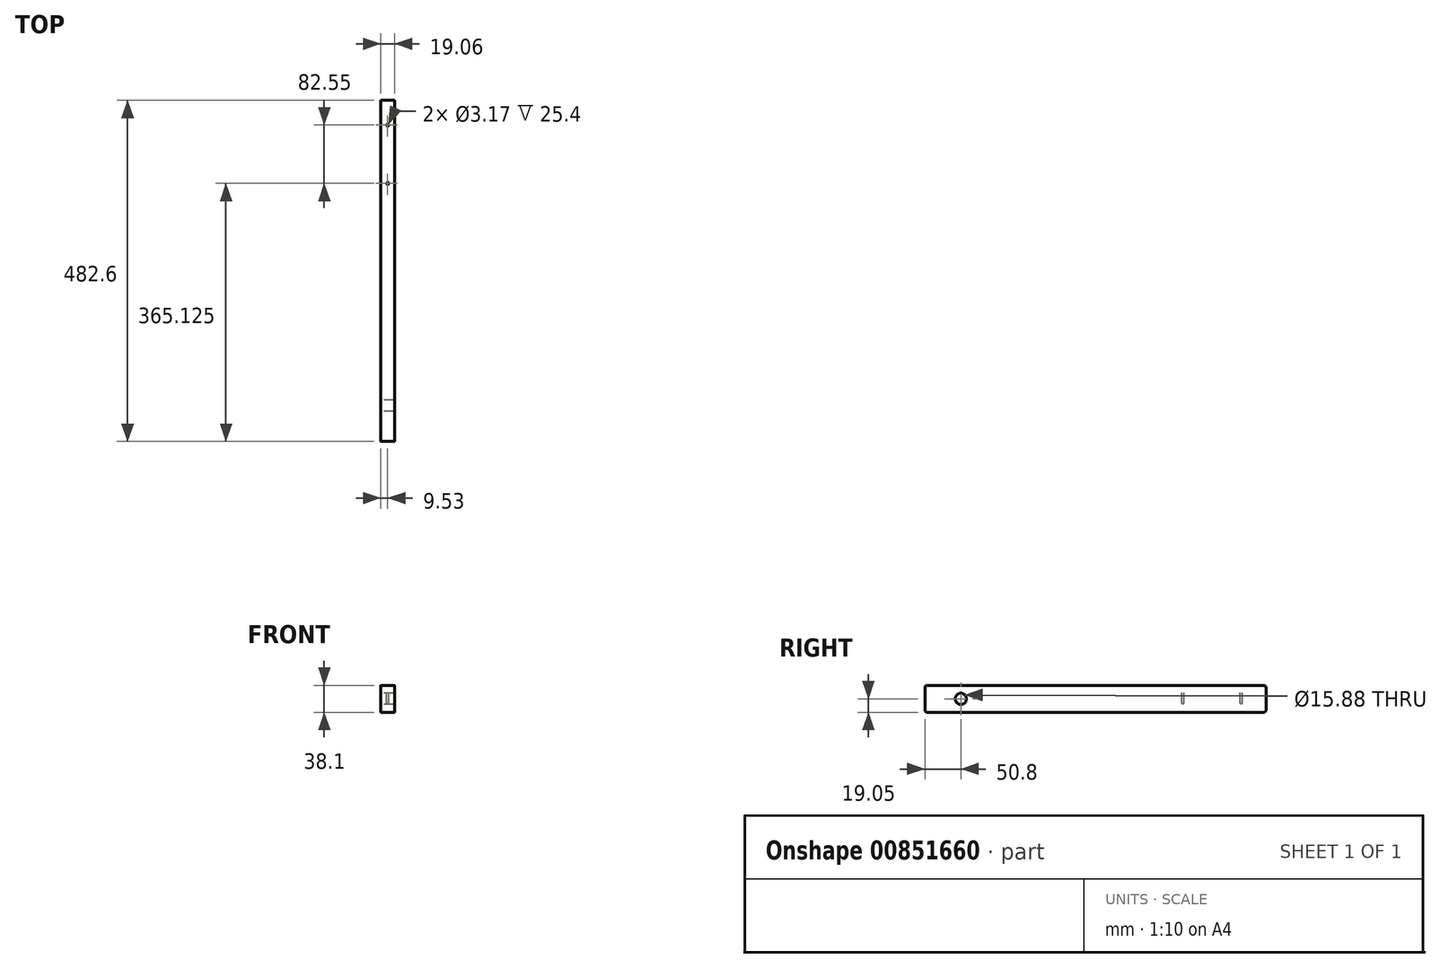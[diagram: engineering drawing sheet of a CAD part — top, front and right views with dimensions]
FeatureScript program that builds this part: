
annotation { "Feature Type Name" : "Feature", "Feature Type Description" : "" }
export const myFeature = defineFeature(function(context is Context, id is Id, definition is map)
    precondition{}
    {
        {
            var Q0;
            Q0=qCreatedBy(makeId("Right.planeOp"),FACE);
            var sketch = newSketch(context, id + "F0", { "sketchPlane" : qUnion([Q0])});
            skLineSegment(sketch, "E0.bottom", {"start": v(431.8, 19.05) * mm, "end": v(-50.8, 19.05) * mm});
            skLineSegment(sketch, "E0.top", {"start": v(431.8, -19.05) * mm, "end": v(-50.8, -19.05) * mm});
            skLineSegment(sketch, "E0.right", {"start": v(-50.8, 19.05) * mm, "end": v(-50.8, -19.05) * mm});
            skPoint(sketch, "E0.middle", {"position": v(0, 0) * mm});
            skCircle(sketch, "E1", {"center": v(0, 0) * mm, "radius": 7.94 * mm});
            skLineSegment(sketch, "E2", {"start": v(0, 0) * mm, "end": v(-50.8, 0) * mm, "construction": true});
            skLineSegment(sketch, "E3", {"start": v(431.8, 19.05) * mm, "end": v(431.8, -19.05) * mm});
            skLineSegment(sketch, "E4", {"start": v(355.6, 19.05) * mm, "end": v(355.6, -19.05) * mm, "construction": true});
            skSolve(sketch);
        }
        {
            var Q0;
            Q0=qSketchRegion(id+"F0",true);
            extrude(context, id + "F1", {"entities" : qUnion([Q0]), "endBound" : BoundingType.SYMMETRIC, "depth" : 19.05 * mm, "offsetDistance" : 25.4 * mm});
        }
        {
            var Q0;
            Q0=makeQuery(id+"F1.opExtrude","SWEPT_FACE",FACE,{"disambiguationData":[OSD([sQuery(id+"F0.wireOp",EDGE,"E0.bottom")])]});
            var sketch = newSketch(context, id + "F2", { "sketchPlane" : qUnion([Q0])});
            skLineSegment(sketch, "E5", {"start": v(-9.53, 355.6) * mm, "end": v(9.53, 355.6) * mm, "construction": true});
            skLineSegment(sketch, "E6", {"start": v(0, 396.88) * mm, "end": v(0, 355.6) * mm, "construction": true});
            skCircle(sketch, "E7", {"center": v(0, 396.88) * mm, "radius": 1.59 * mm});
            skCircle(sketch, "E8", {"center": v(0, 314.33) * mm, "radius": 1.59 * mm});
            skLineSegment(sketch, "E9", {"start": v(0, 355.6) * mm, "end": v(0, 314.33) * mm, "construction": true});
            skSolve(sketch);
        }
        {
            var Q0;
            Q0=qSketchRegion(id+"F2",true);
            extrude(context, id + "F3", {"entities" : qUnion([Q0]), "operationType" : NewBodyOperationType.REMOVE, "oppositeDirection" : true, "depth" : 25.4 * mm, "offsetDistance" : 25.4 * mm});
        }
        {
            var Q0;
            Q0=makeQuery(id+"F1.opExtrude","SWEPT_EDGE",EDGE,{"disambiguationData":[OSD([sQuery(id+"F0.wireOp",EDGE,"E0.top"),sQuery(id+"F0.wireOp",EDGE,"E3")])]});
            fillet(context, id + "F4", {"entities" : qUnion([Q0]), "radius" : 3.17 * mm, "tangentPropagation" : true, "allowEdgeOverflow" : false});
        }
        {
            var Q0;
            Q0=makeQuery(id+"F1.opExtrude","SWEPT_EDGE",EDGE,{"disambiguationData":[OSD([sQuery(id+"F0.wireOp",EDGE,"E0.bottom"),sQuery(id+"F0.wireOp",EDGE,"E3")])]});
            var Q1;
            Q1=makeQuery(id+"F1.opExtrude","SWEPT_EDGE",EDGE,{"disambiguationData":[OSD([sQuery(id+"F0.wireOp",EDGE,"E0.top"),sQuery(id+"F0.wireOp",EDGE,"vXA6KAkI-sKuc-wAv4-CYPb-lMJrvv2wS4qW")])]});
            var Q2;
            Q2=makeQuery(id+"F1.opExtrude","SWEPT_EDGE",EDGE,{"disambiguationData":[OSD([sQuery(id+"F0.wireOp",EDGE,"E0.bottom"),sQuery(id+"F0.wireOp",EDGE,"vXA6KAkI-sKuc-wAv4-CYPb-lMJrvv2wS4qW")])]});
            fillet(context, id + "F5", {"entities" : qUnion([Q0, Q1, Q2]), "radius" : 3.17 * mm, "tangentPropagation" : true, "allowEdgeOverflow" : false});
        }
    });
